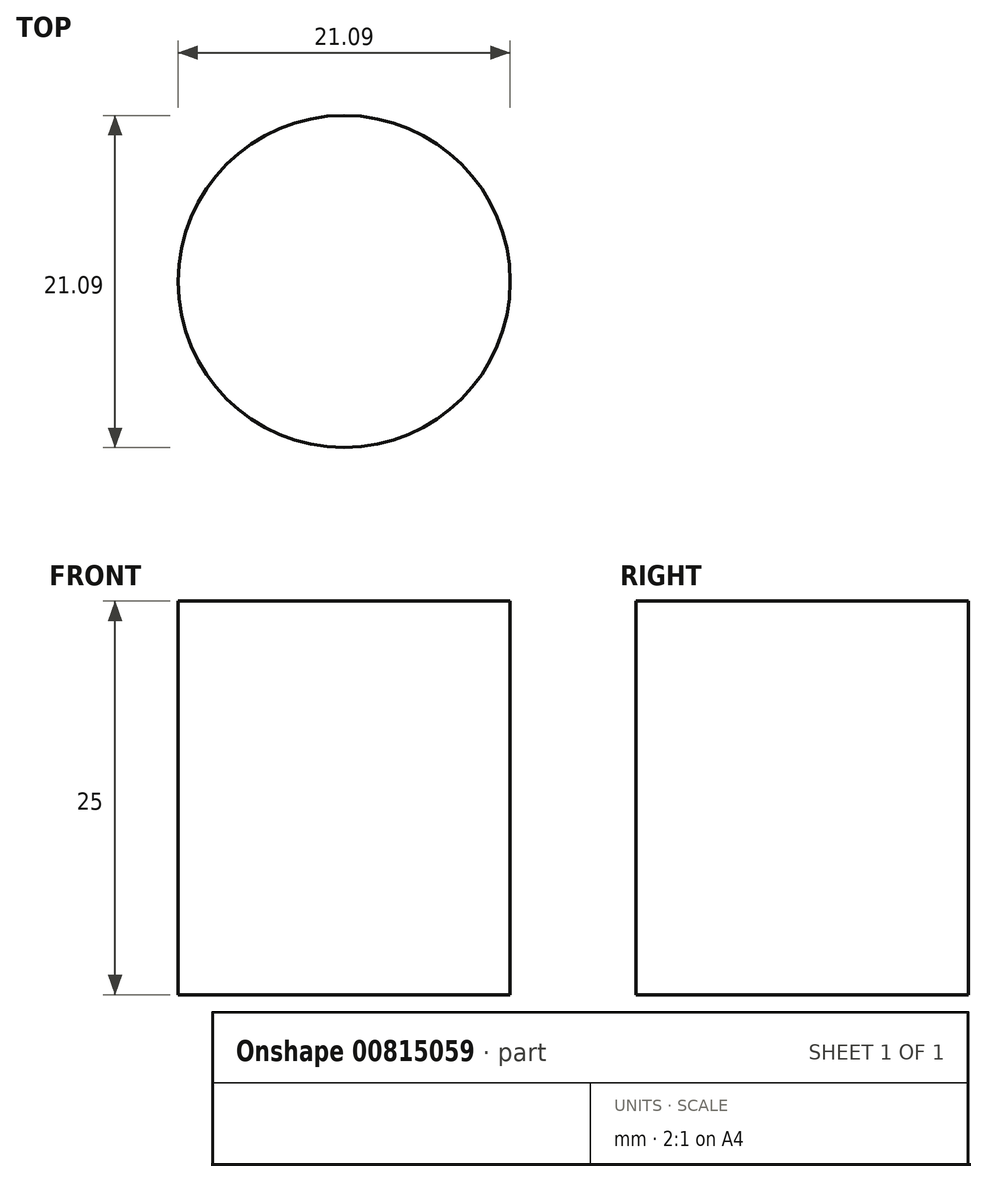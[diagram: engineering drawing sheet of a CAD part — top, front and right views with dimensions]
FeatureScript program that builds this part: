
annotation { "Feature Type Name" : "Feature", "Feature Type Description" : "" }
export const myFeature = defineFeature(function(context is Context, id is Id, definition is map)
    precondition{}
    {
        {
            var Q0;
            Q0=qCreatedBy(makeId("Top.planeOp"),FACE);
            var sketch = newSketch(context, id + "F0", { "sketchPlane" : qUnion([Q0])});
            skCircle(sketch, "E0", {"center": v(-25.72, 35.2) * mm, "radius": 10.54 * mm});
            skCircle(sketch, "E1", {"center": v(24.33, 20.58) * mm, "radius": 10.54 * mm});
            skSolve(sketch);
        }
        {
            var Q0;
            Q0=makeQuery(id+"F0.imprint","IMPRINT",FACE,{"disambiguationData":[TD([[makeQuery(id+"F0.imprint","IMPRINT",EDGE,{"derivedFrom":sQuery(id+"F0.wireOp",EDGE,"E0")}),1.0]])]});
            extrude(context, id + "F1", {"entities" : qUnion([Q0]), "depth" : 25 * mm, "offsetDistance" : 25 * mm});
        }
    });
